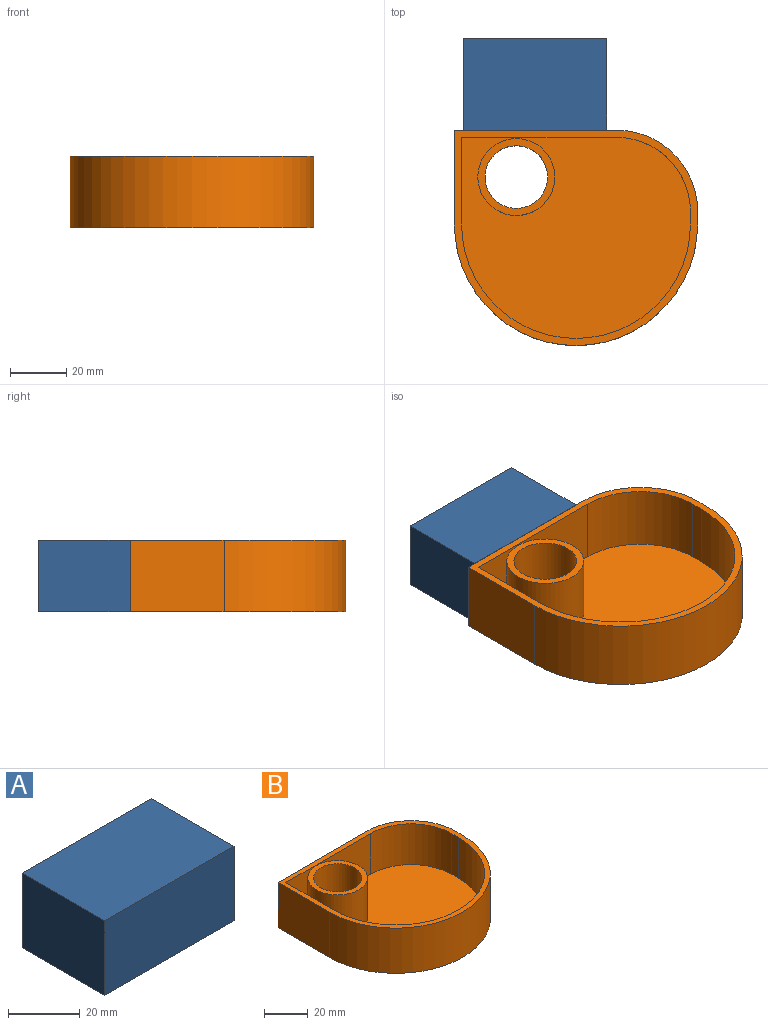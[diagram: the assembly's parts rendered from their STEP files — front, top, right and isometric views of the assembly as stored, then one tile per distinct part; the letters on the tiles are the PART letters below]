
ASSEMBLY  parts=2 mates=1
PART A: 6 faces, bbox 50.8x32.6x25.4 mm
  f0: plane 50.8x25.4mm, normal (0,1,0), area 1290.3mm2, adj f1,f3,f4,f5
  f1: plane 32.57x25.4mm, normal (-1,0,0), area 827.3mm2, adj f0,f2,f4,f5
  f2: plane 50.8x25.4mm, normal (0,-1,0), area 1290.3mm2, adj f1,f3,f4,f5
  f3: plane 32.57x25.4mm, normal (1,0,0), area 827.3mm2, adj f0,f2,f4,f5
  f4: plane 50.8x32.57mm, normal (0,0,1), area 1654.5mm2, adj f0,f1,f2,f3
  f5: plane 50.8x32.57mm, normal (0,0,-1), area 1654.5mm2, adj f0,f1,f2,f3
PART B: 16 faces, bbox 86.3x76.4x25.4 mm
  f0: plane 27.28x27.28mm, normal (0,0,1), area 197.4mm2, adj f5,f13
  f1: cylinder r=43.14mm len=86.28mm, axis (0,0,-1), area 3442.4mm2, adj f2,f4,f6,f7
  f2: plane 25.4x4.46mm, normal (1,0,0), area 113.3mm2, adj f1,f6,f7,f8
  f3: plane 57.46x25.4mm, normal (0,1,0), area 1459.4mm2, adj f4,f6,f7,f8
  f4: plane 33.28x25.4mm, normal (-1,0,0), area 845.4mm2, adj f1,f3,f6,f7
  f5: cylinder r=11.1mm len=25.4mm, axis (0,0,-1), area 1771.3mm2, adj f0,f7
  f6: plane 86.28x76.42mm, normal (0,0,1), area 679.4mm2, adj f1,f2,f3,f4,f8,f9,f10,f11
  f7: plane 86.28x76.42mm, normal (0,0,-1), area 5229.6mm2, adj f1,f2,f3,f4,f5,f8
  f8: cylinder r=28.82mm len=28.82mm, axis (0,0,1), area 1149.9mm2, adj f2,f3,f6,f7
  f9: cylinder r=40.6mm len=81.2mm, axis (0,0,-1), area 2915.7mm2, adj f6,f10,f12,f14
  f10: plane 22.86x4.46mm, normal (-1,0,0), area 102mm2, adj f6,f9,f14,f15
  f11: plane 54.92x22.86mm, normal (0,-1,0), area 1255.4mm2, adj f6,f12,f14,f15
  f12: plane 30.74x22.86mm, normal (1,0,0), area 702.8mm2, adj f6,f9,f11,f14
  f13: cylinder r=13.64mm len=27.28mm, axis (0,0,-1), area 1959mm2, adj f0,f14
  f14: plane 81.2x71.34mm, normal (0,0,1), area 4352.8mm2, adj f9,f10,f11,f12,f13,f15
  f15: cylinder r=26.28mm len=26.28mm, axis (0,0,1), area 943.7mm2, adj f6,f10,f11,f14
PLACE A t=(8.19,18.33,-39.83)mm
PLACE B t=(-21.62,-13.96,-39.83)mm
MATE fastened A.f2 <-> B.f3  axis (0,-1,0) through (-97.64,-31.19,-27.13)mm
